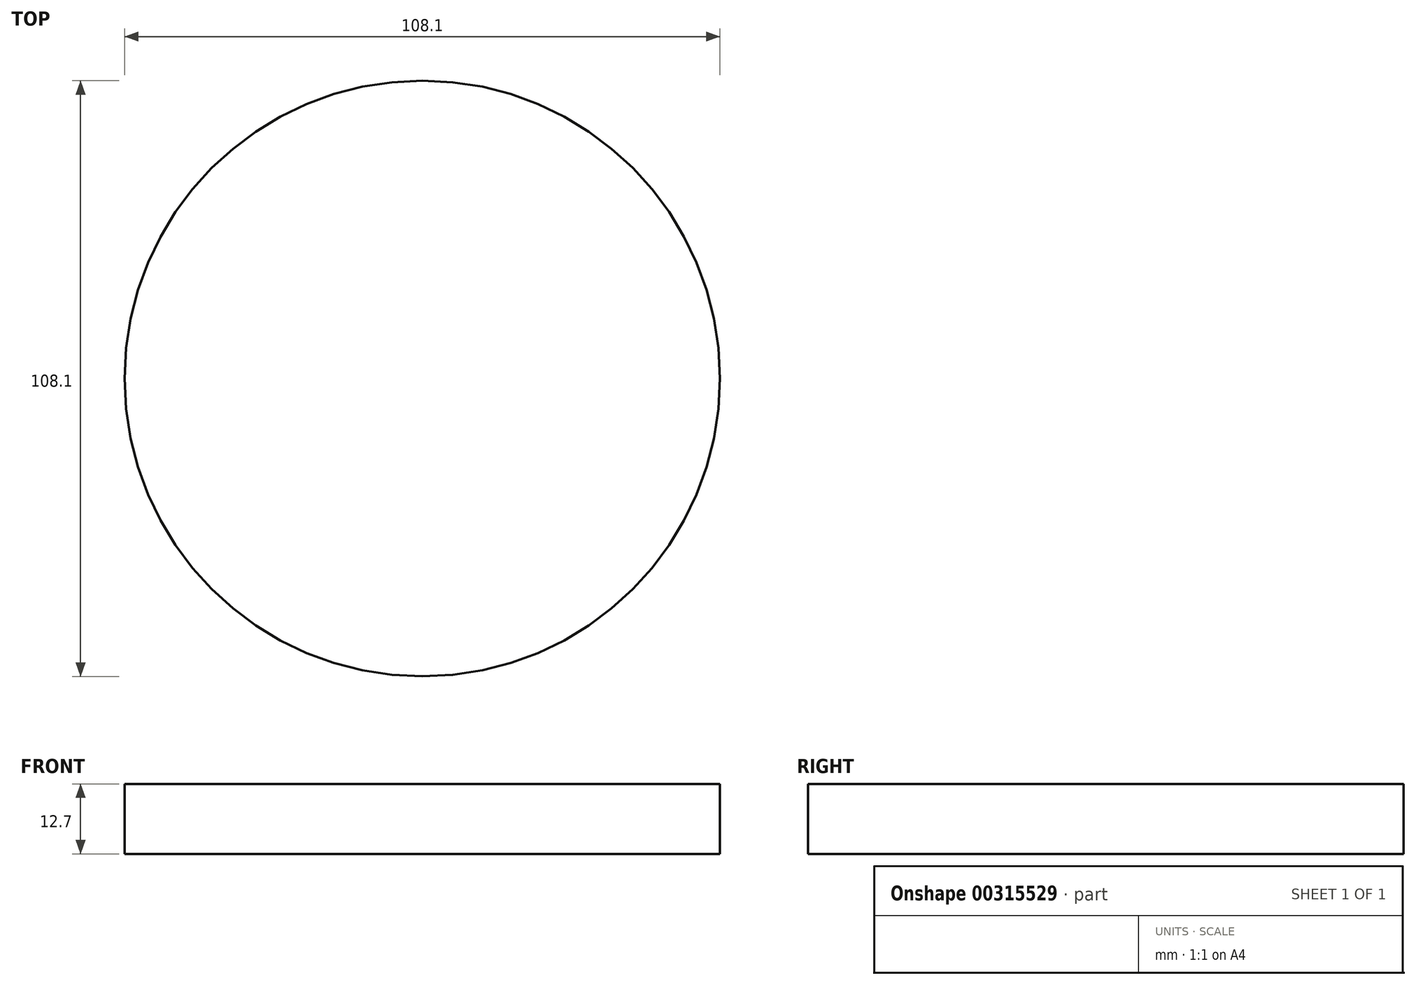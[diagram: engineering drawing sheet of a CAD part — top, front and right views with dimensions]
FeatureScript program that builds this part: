
annotation { "Feature Type Name" : "Feature", "Feature Type Description" : "" }
export const myFeature = defineFeature(function(context is Context, id is Id, definition is map)
    precondition{}
    {
        {
            var Q0;
            Q0=qCreatedBy(makeId("Top.planeOp"),FACE);
            var sketch = newSketch(context, id + "F0", { "sketchPlane" : qUnion([Q0])});
            skCircle(sketch, "E0", {"center": v(0, 0) * mm, "radius": 54.05 * mm});
            skSolve(sketch);
        }
        {
            var Q0;
            Q0=makeQuery(id+"F0.imprint","IMPRINT",FACE,{"disambiguationData":[TD([[makeQuery(id+"F0.imprint","IMPRINT",EDGE,{"derivedFrom":sQuery(id+"F0.wireOp",EDGE,"E0")}),1.0]])]});
            extrude(context, id + "F1", {"entities" : qUnion([Q0]), "depth" : 12.7 * mm});
        }
    });
